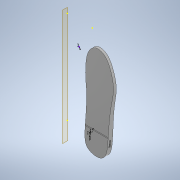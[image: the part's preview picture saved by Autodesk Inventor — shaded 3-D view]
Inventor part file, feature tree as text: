
AUTODESK INVENTOR PART (.ipt)
format: ipt  version: 2022 (Build 260153000, 153)  size: 4,192,256 bytes
history: native  units: mm
features: sketch x26, extrude x21, fillet x15, chamfer x9, other x2
ambient origin geometry x8: Origin, YZ Plane, XZ Plane, XY Plane, X Axis, Y Axis, Z Axis, Center Point
bodies: Solid1 (feature_tree)
feature tree (73):
  extrude  "Extrusion1"  Depth=0.698132mm
  sketch  "Sketch2"  dims[d52=15.0mm d53=0.0mm d54=13.0mm]
  extrude  "Extrusion2"  Depth=13.0mm
  chamfer  "Chamfer1"  [1 undecoded]
  sketch  "Sketch4"  dims[d56=265.0mm d57=0.0mm d58=0.0mm]
  extrude  "Extrusion3"  Depth=20.0mm
  extrude  "Extrusion4"  Depth=52.15mm
  extrude  "Extrusion5"  Depth=82.0mm
  sketch  "Sketch6"  dims[d63=52.15mm d64=52.15mm]
  extrude  "Extrusion6"  Depth=10.0mm
  extrude  "Extrusion7"  Depth=10.0mm TaperAngle=0.0deg
  chamfer  "Chamfer2"  Distance=11.0mm
  extrude  "Extrusion8"  Depth=8.0mm TaperAngle=0.0deg
  chamfer  "Chamfer3"  [1 undecoded]
  extrude  "Extrusion9"  Depth=55.0mm TaperAngle=0.0deg
  fillet  "Fillet2"  Radius=1.0mm
  fillet  "Fillet3"  Radius=26.5mm
  fillet  "Fillet4"  Radius=33.0mm
  extrude  "Extrusion10"  Depth=1.2mm
  chamfer  "Chamfer4"  Distance=7.15mm
  sketch  "Sketch10"  dims[d74=15.0mm d75=8.0mm d76=0.0mm]
  extrude  "Extrusion11"  Depth=10.0mm
  fillet  "Fillet6"  Radius=18.0mm
  fillet  "Fillet7"  Radius=9.0mm
  extrude  "Extrusion12"  Depth=10.0mm TaperAngle=45.0deg
  fillet  "Fillet8"  Radius=33.0mm
  fillet  "Fillet9"  Radius=3.0mm
  sketch  "Sketch13"  dims[d81=5.0mm d82=55.0mm d83=0.0mm]
  extrude  "Extrusion13"  TaperAngle=90.0deg  [1 undecoded]
  sketch  "Sketch15"  dims[d90=0.25mm d91=2.0mm d92=45.0deg d93=26.5mm d94=33.0mm]
  fillet  "Fillet10"  Radius=25.0mm
  chamfer  "Chamfer5"  Distance=0.5mm
  extrude  "Extrusion14"  Depth=10.0mm
  fillet  "Fillet11"  Radius=0.5mm
  sketch  "Sketch17"  dims[d98=5.0mm]
  sketch  "Sketch18"  dims[d99=2.0mm]
  extrude  "Extrusion16"  Depth=10.0mm
  sketch  "Sketch22"  dims[d101=2.0mm]
  extrude  "Extrusion18"  Depth=10.0mm
  chamfer  "Chamfer8"  Distance=2.0mm
  extrude  "Extrusion20"  Depth=10.0mm
  extrude  "Extrusion21"  Depth=10.0mm
  chamfer  "Chamfer11"  [1 undecoded]
  chamfer  "Chamfer12"  Distance=27.0mm
  fillet  "Fillet18"  Radius=1.0mm
  fillet  "Fillet19"  Radius=2.0mm
  sketch  "Sketch26"  dims[d105=5.15mm]
  extrude  "Extrusion22"  Depth=10.0mm
  fillet  "Fillet21"  Radius=3.70509mm
  fillet  "Fillet22"  Radius=0.5mm
  fillet  "Fillet23"  Radius=0.5mm
  extrude  "Extrusion23"  TaperAngle=0.0deg  [1 undecoded]
  fillet  "Fillet24"  [1 undecoded]
  extrude  "Extrusion24"  TaperAngle=0.0deg  [1 undecoded]
  chamfer  "Chamfer13"  Distance=1.0mm
  sketch  "Sketch1"  dims[d7=0.0mm d32=0.698132mm]
  other  "Image1"
  sketch  "Sketch3"  dims[d55=75.0mm]
  sketch  "Sketch5"  dims[d59=2.0mm d60=2.0mm d61=45.0deg d62=20.0mm]
  sketch  "Sketch7"  dims[d65=21.25mm d66=82.0mm]
  sketch  "Sketch8"  dims[d67=8.0mm d68=10.0mm]
  sketch  "Sketch9"  dims[d69=2.0mm d70=10.0mm d71=0.0mm d72=11.0mm d73=0.0mm]
  other  "Image2"
  sketch  "Sketch11"  dims[d77=4.0mm]
  sketch  "Sketch12"  dims[d78=1.0mm d79=0.0mm d80=0.0mm]
  sketch  "Sketch14"  dims[d84=5.0mm d85=2.0mm d86=45.0deg d88=1.0mm d89=0.0mm]
  sketch  "Sketch16"  dims[d95=6.0mm d96=0.0mm d97=1.2mm]
  sketch  "Sketch20"  dims[d100=0.5mm]
  sketch  "Sketch23"  dims[d102=5.15mm]
  sketch  "Sketch24"  dims[d103=90.0mm]
  sketch  "Sketch25"  dims[d104=272.0mm]
  sketch  "Sketch27"  dims[d106=35.0mm]
  sketch  "Sketch28"  dims[d107=2.0mm d108=7.15mm d109=61.0mm d110=18.0mm d111=9.0mm d112=0.0mm d113=0.5mm d114=2.0mm d115=45.0deg d124=33.0mm d141=3.0mm d143=90.0deg d144=25.0mm d145=2.0mm d146=0.0mm d147=0.0mm d148=0.5mm d149=1.0mm d150=0.5mm d151=4.0mm d152=40.0mm d153=2.0mm d154=0.0mm d155=0.5mm d156=0.5mm d157=0.0mm d158=27.0mm d159=1.0mm d160=0.0mm d161=2.0mm d162=1.0mm d163=3.70509mm d164=0.5mm d165=0.5mm d166=2.0mm d167=45.0deg d168=0.0mm d169=0.0mm d170=0.0mm d171=1.0mm d172=0.0mm d173=19.0mm d174=5.5mm d175=5.5mm d176=19.0mm d177=62.65mm d178=51.65mm d179=21.0mm d180=1.0mm d181=0.0mm d183=0.5mm d184=8.0mm d195=7.0mm d196=8.0mm d197=4.0mm d198=25.0mm d199=0.0mm d213=3.0mm d214=17.6mm d216=32.75mm d217=1.9mm d218=5.0mm d219=4.0mm d220=0.0mm d221=2.0mm d222=2.0mm d223=45.0deg d224=4.0mm d225=2.0mm d226=32.75mm d229=10.0mm d230=0.0mm d233=0.0mm d234=10.0mm d235=0.0mm d242=3.0mm d243=1.5mm d244=45.0deg d245=3.0mm d246=1.5mm d247=45.0deg d248=0.5mm d249=1.0mm d250=1.5mm d251=5.0mm d252=0.0mm d254=0.0mm d255=0.0mm d256=0.5mm d257=0.5mm d258=0.5mm d259=0.0mm d260=0.0mm d261=125.0mm d263=2.85mm d264=5.0mm d265=26.075mm d266=26.075mm d267=6.0mm d268=2.85mm d269=5.0mm d270=2.85mm d271=3.0mm d272=5.0mm d273=5.0mm d274=10.0mm d275=0.0mm d276=0.5mm d277=1.0mm d278=45.0deg d279=15.25mm d280=3.0mm d87=0.0mm]
note: 7 required parameter values undecoded (feature->parameter linkage not recoverable at this tier; creation-order binding heuristic only, values carry confidence <= 0.55)
